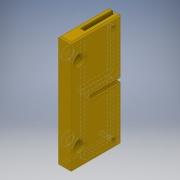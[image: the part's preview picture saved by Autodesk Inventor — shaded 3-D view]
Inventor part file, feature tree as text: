
AUTODESK INVENTOR PART (.ipt)
format: ipt  version: 2019 (Build 230136000, 136)  size: 374,784 bytes
history: native  units: mm
features: sketch x5, extrude x4, chamfer x2, hole x1
ambient origin geometry x8: Origin, YZ Plane, XZ Plane, XY Plane, X Axis, Y Axis, Z Axis, Center Point
bodies: Solid1 (feature_tree)
feature tree (12):
  extrude  "Extrusion1"  Depth=89.0mm
  extrude  "Extrusion2"  Depth=3.3mm
  extrude  "Extrusion3"  Depth=25.0mm
  hole  "Hole1"  [1 undecoded]
  chamfer  "Chamfer1"  Distance=19.5mm
  extrude  "Extrusion4"  Depth=1.0mm TaperAngle=45.0deg
  chamfer  "Chamfer2"  Distance=6.0mm
  sketch  "Sketch1"  dims[d0=10.0mm d1=89.0mm]
  sketch  "Sketch2"  dims[d2=40.0mm d3=0.0mm d4=3.3mm]
  sketch  "Sketch3"  dims[d5=26.0mm d6=0.0mm]
  sketch  "Sketch4"  dims[d8=3.0mm d9=6.0mm d10=4.0mm d11=2.0mm d12=90.0deg d13=26.75mm d14=0.0mm d15=25.0mm]
  sketch  "Sketch5"  dims[d16=3.2mm d17=16.0mm d18=0.0mm d19=19.5mm d20=1.0mm d21=2.0mm d22=45.0deg d23=6.0mm d24=33.0mm d25=15.0mm d26=15.0mm d27=10.0mm d28=0.0mm d29=2.0mm d30=2.0mm d31=45.0deg]
note: 1 required parameter value undecoded (feature->parameter linkage not recoverable at this tier; creation-order binding heuristic only, values carry confidence <= 0.55)
